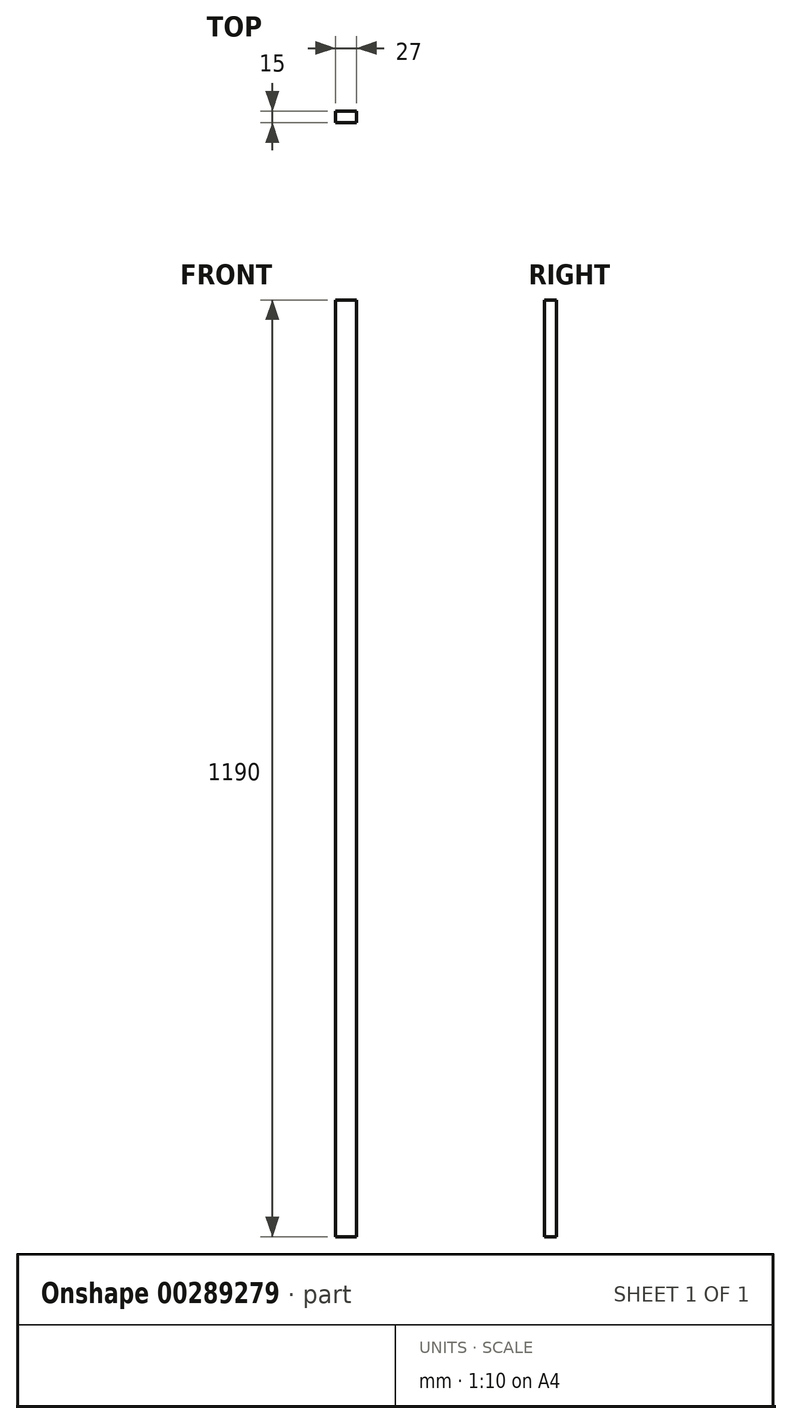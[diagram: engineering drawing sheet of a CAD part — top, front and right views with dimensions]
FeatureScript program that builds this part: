
annotation { "Feature Type Name" : "Feature", "Feature Type Description" : "" }
export const myFeature = defineFeature(function(context is Context, id is Id, definition is map)
    precondition{}
    {
        {
            var Q0;
            Q0=qCreatedBy(makeId("Top.planeOp"),FACE);
            var sketch = newSketch(context, id + "F0", { "sketchPlane" : qUnion([Q0])});
            skLineSegment(sketch, "E0.bottom", {"start": v(0, -5.78) * mm, "end": v(27, -5.78) * mm});
            skLineSegment(sketch, "E0.top", {"start": v(0, -20.78) * mm, "end": v(27, -20.78) * mm});
            skLineSegment(sketch, "E0.left", {"start": v(0, -5.78) * mm, "end": v(0, -20.78) * mm});
            skLineSegment(sketch, "E0.right", {"start": v(27, -5.78) * mm, "end": v(27, -20.78) * mm});
            skSolve(sketch);
        }
        {
            var Q0;
            Q0=makeQuery(id+"F0.imprint","IMPRINT",FACE,{"disambiguationData":[TD([[makeQuery(id+"F0.imprint","IMPRINT",EDGE,{"derivedFrom":sQuery(id+"F0.wireOp",EDGE,"E0.bottom")}),-1.0]])]});
            extrude(context, id + "F1", {"entities" : qUnion([Q0]), "depth" : 1190 * mm});
        }
    });
